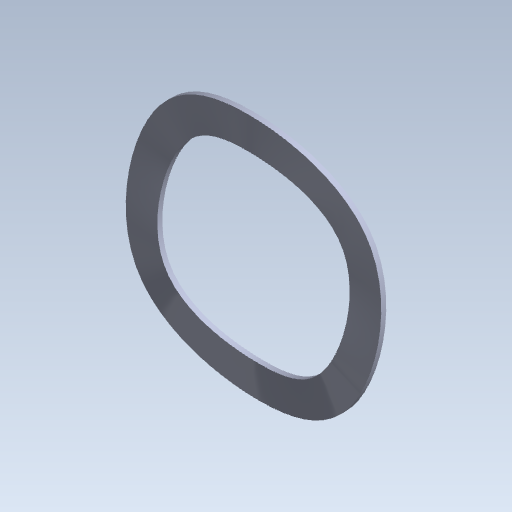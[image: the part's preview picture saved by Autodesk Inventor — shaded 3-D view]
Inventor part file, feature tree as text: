
AUTODESK INVENTOR PART (.ipt)
format: ipt  version: 2020 (Build 240168000, 168)  size: 95,744 bytes
history: native  units: mm (DEFAULTED — no unit token found)
features: loft x1
ambient origin geometry x8: Origin, YZ Plane, XZ Plane, XY Plane, X Axis, Y Axis, Z Axis, Center Point
bodies: Solid1 (feature_tree)
feature tree (1):
  loft  "Loft1"
